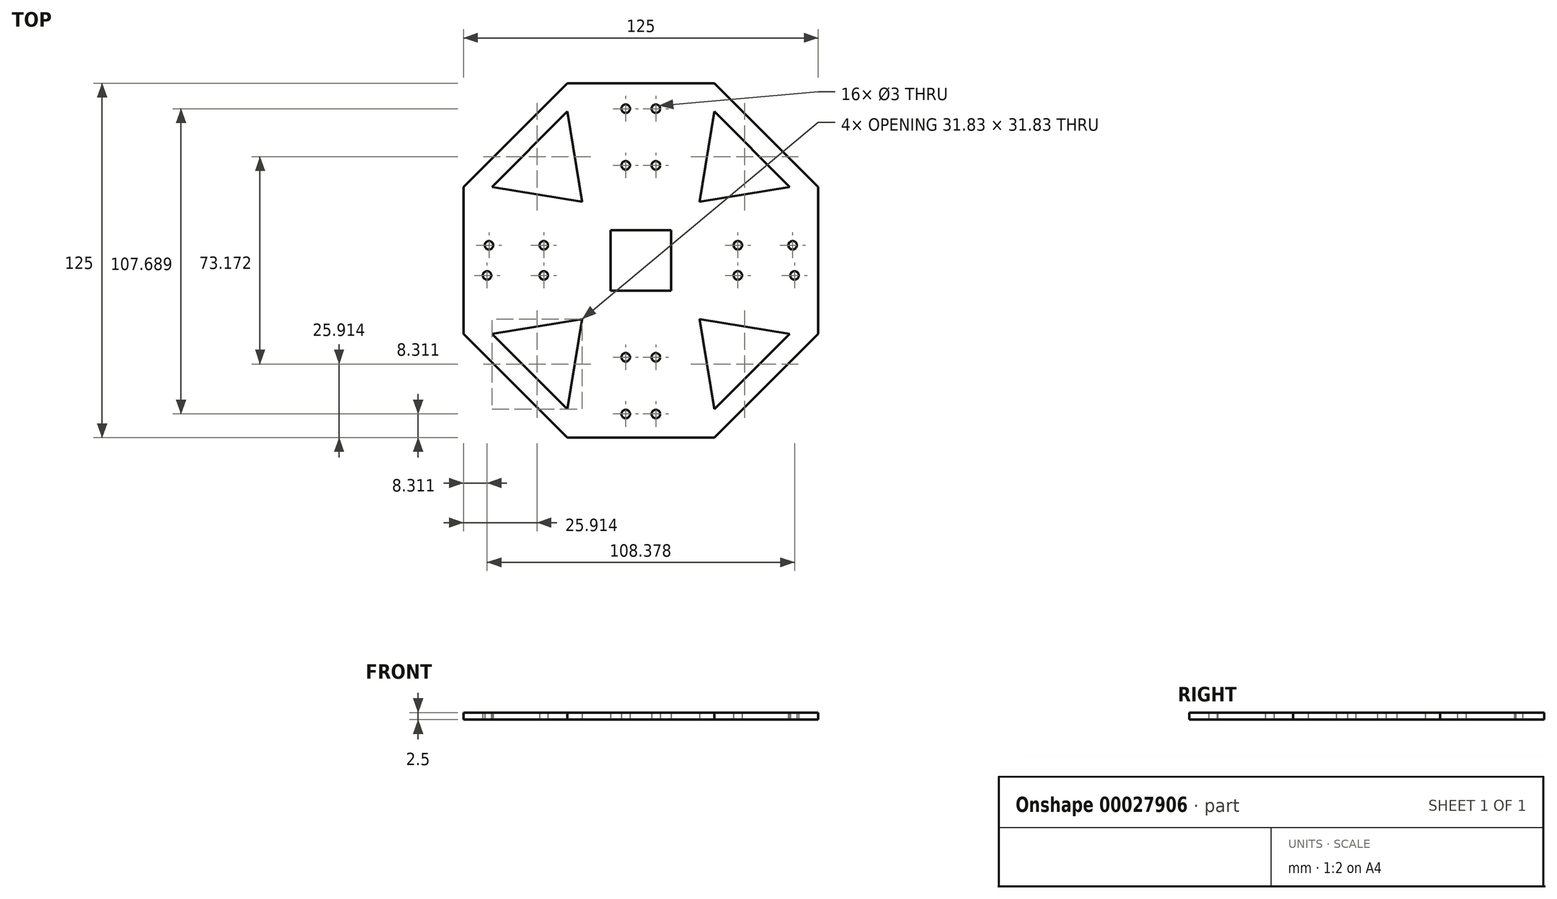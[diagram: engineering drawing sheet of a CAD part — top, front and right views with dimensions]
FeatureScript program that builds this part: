
annotation { "Feature Type Name" : "Feature", "Feature Type Description" : "" }
export const myFeature = defineFeature(function(context is Context, id is Id, definition is map)
    precondition{}
    {
        {
            var Q0;
            Q0=qCreatedBy(makeId("Top.planeOp"),FACE);
            var sketch = newSketch(context, id + "F0", { "sketchPlane" : qUnion([Q0])});
            skCircle(sketch, "E0.cCircle", {"center": v(0, 0) * mm, "radius": 62.5 * mm, "construction": true});
            skLineSegment(sketch, "E0.0", {"start": v(-25.89, 62.5) * mm, "end": v(25.89, 62.5) * mm});
            skLineSegment(sketch, "E0.1", {"start": v(25.89, 62.5) * mm, "end": v(62.5, 25.89) * mm});
            skLineSegment(sketch, "E0.2", {"start": v(62.5, 25.89) * mm, "end": v(62.5, -25.89) * mm});
            skLineSegment(sketch, "E0.3", {"start": v(62.5, -25.89) * mm, "end": v(25.89, -62.5) * mm});
            skLineSegment(sketch, "E0.4", {"start": v(25.89, -62.5) * mm, "end": v(-25.89, -62.5) * mm});
            skLineSegment(sketch, "E0.5", {"start": v(-25.89, -62.5) * mm, "end": v(-62.5, -25.89) * mm});
            skLineSegment(sketch, "E0.6", {"start": v(-62.5, -25.89) * mm, "end": v(-62.5, 25.89) * mm});
            skLineSegment(sketch, "E0.7", {"start": v(-62.5, 25.89) * mm, "end": v(-25.89, 62.5) * mm});
            skPoint(sketch, "E0.0.midPoint", {"position": v(0, 62.5) * mm});
            skLineSegment(sketch, "E1.rect.bottom", {"start": v(10.67, 10.67) * mm, "end": v(-10.67, 10.67) * mm});
            skLineSegment(sketch, "E1.rect.top", {"start": v(10.67, -10.67) * mm, "end": v(-10.67, -10.67) * mm});
            skLineSegment(sketch, "E1.rect.left", {"start": v(10.67, 10.67) * mm, "end": v(10.67, -10.67) * mm});
            skLineSegment(sketch, "E1.rect.right", {"start": v(-10.67, 10.67) * mm, "end": v(-10.67, -10.67) * mm});
            skLineSegment(sketch, "E2", {"start": v(-10.67, 20.67) * mm, "end": v(-10.67, 52.5) * mm});
            skLineSegment(sketch, "E3", {"start": v(-10.67, -52.5) * mm, "end": v(-10.67, -20.67) * mm});
            skLineSegment(sketch, "E4", {"start": v(-10.67, -20.67) * mm, "end": v(-20.67, -10.67) * mm});
            skLineSegment(sketch, "E5", {"start": v(-20.67, -10.67) * mm, "end": v(-20.67, 9.38) * mm});
            skLineSegment(sketch, "E6", {"start": v(-20.67, 9.38) * mm, "end": v(-10.67, 20.67) * mm});
            skLineSegment(sketch, "E7.1.3", {"start": v(10.67, 52.5) * mm, "end": v(10.67, 20.67) * mm});
            skLineSegment(sketch, "E7.1.4", {"start": v(10.67, 20.67) * mm, "end": v(20.67, 10.67) * mm});
            skLineSegment(sketch, "E7.1.5", {"start": v(20.67, 10.67) * mm, "end": v(20.67, -9.38) * mm});
            skLineSegment(sketch, "E7.1.6", {"start": v(20.67, -9.38) * mm, "end": v(10.67, -20.67) * mm});
            skLineSegment(sketch, "E7.1.7", {"start": v(10.67, -20.67) * mm, "end": v(10.67, -52.5) * mm});
            skLineSegment(sketch, "E8", {"start": v(0, 0) * mm, "end": v(0, -60.07) * mm, "construction": true});
            skLineSegment(sketch, "E9", {"start": v(0, -77.84) * mm, "end": v(0, 78.09) * mm, "construction": true});
            skLineSegment(sketch, "E10", {"start": v(0, 0) * mm, "end": v(98.82, 0) * mm, "construction": true});
            skPoint(sketch, "E10.endSnap0", {"position": v(62.5, 0) * mm});
            skLineSegment(sketch, "E11", {"start": v(98.82, 0) * mm, "end": v(-127.93, 0) * mm, "construction": true});
            skCircle(sketch, "E12", {"center": v(-5.32, -54.19) * mm, "radius": 1.5 * mm});
            skCircle(sketch, "E13.MirrorC", {"center": v(5.32, -54.19) * mm, "radius": 1.5 * mm});
            skCircle(sketch, "E14.0.1.0", {"center": v(-5.32, -34.19) * mm, "radius": 1.5 * mm});
            skCircle(sketch, "E14.0.1.1", {"center": v(5.32, -34.19) * mm, "radius": 1.5 * mm});
            skCircle(sketch, "E15.1.0", {"center": v(34.19, 5.32) * mm, "radius": 1.5 * mm});
            skCircle(sketch, "E15.1.1", {"center": v(34.19, -5.32) * mm, "radius": 1.5 * mm});
            skCircle(sketch, "E15.1.2", {"center": v(53.5, 5.32) * mm, "radius": 1.5 * mm});
            skCircle(sketch, "E15.1.3", {"center": v(54.19, -5.32) * mm, "radius": 1.5 * mm});
            skLineSegment(sketch, "E15.1.4", {"start": v(78.86, 3.3) * mm, "end": v(10.67, 1.61) * mm, "construction": true});
            skLineSegment(sketch, "E15.2.4", {"start": v(-0.92, 80.21) * mm, "end": v(2.96, -75.67) * mm, "construction": true});
            skLineSegment(sketch, "E15.3.4", {"start": v(-77.84, 1.03) * mm, "end": v(78.09, 1.03) * mm, "construction": true});
            skPoint(sketch, "E15.center", {"position": v(0.51, 0) * mm});
            skPoint(sketch, "E15.2.3.center.orphan", {"position": v(7.62, 55.69) * mm});
            skLineSegment(sketch, "E16.trimOffspring", {"start": v(1.04, 1.37) * mm, "end": v(-77.02, -0.57) * mm, "construction": true});
            skCircle(sketch, "E17.MirrorC", {"center": v(-34.19, 5.32) * mm, "radius": 1.5 * mm});
            skCircle(sketch, "E18.MirrorC", {"center": v(-53.5, 5.32) * mm, "radius": 1.5 * mm});
            skCircle(sketch, "E19.MirrorC", {"center": v(-54.19, -5.32) * mm, "radius": 1.5 * mm});
            skCircle(sketch, "E20.MirrorC", {"center": v(-34.19, -5.32) * mm, "radius": 1.5 * mm});
            skCircle(sketch, "E21", {"center": v(-5.32, 53.5) * mm, "radius": 1.5 * mm});
            skPoint(sketch, "E22.MirrorC.center.orphan", {"position": v(6.6, 53.16) * mm});
            skCircle(sketch, "E23.MirrorC", {"center": v(5.32, 53.5) * mm, "radius": 1.5 * mm});
            skCircle(sketch, "E24.0.1.0", {"center": v(-5.32, 33.5) * mm, "radius": 1.5 * mm});
            skCircle(sketch, "E24.0.1.1", {"center": v(5.32, 33.5) * mm, "radius": 1.5 * mm});
            skLineSegment(sketch, "E24.direction1", {"start": v(-5.32, 53.5) * mm, "end": v(18.4, 53.5) * mm, "construction": true});
            skLineSegment(sketch, "E24.direction2", {"start": v(-5.32, 53.5) * mm, "end": v(-5.32, 33.5) * mm, "construction": true});
            skLineSegment(sketch, "E25", {"start": v(-52.5, -25.89) * mm, "end": v(-25.89, -52.5) * mm});
            skLineSegment(sketch, "E26", {"start": v(-25.89, -52.5) * mm, "end": v(-20.67, -20.67) * mm});
            skLineSegment(sketch, "E27", {"start": v(-20.67, -20.67) * mm, "end": v(-52.5, -25.89) * mm});
            skLineSegment(sketch, "E28.1.0", {"start": v(25.89, -52.5) * mm, "end": v(52.5, -25.89) * mm});
            skLineSegment(sketch, "E28.1.1", {"start": v(52.5, -25.89) * mm, "end": v(20.67, -20.67) * mm});
            skLineSegment(sketch, "E28.1.2", {"start": v(20.67, -20.67) * mm, "end": v(25.89, -52.5) * mm});
            skLineSegment(sketch, "E28.2.0", {"start": v(52.5, 25.89) * mm, "end": v(25.89, 52.5) * mm});
            skLineSegment(sketch, "E28.2.1", {"start": v(25.89, 52.5) * mm, "end": v(20.67, 20.67) * mm});
            skLineSegment(sketch, "E28.2.2", {"start": v(20.67, 20.67) * mm, "end": v(52.5, 25.89) * mm});
            skLineSegment(sketch, "E28.3.0", {"start": v(-25.89, 52.5) * mm, "end": v(-52.5, 25.89) * mm});
            skLineSegment(sketch, "E28.3.1", {"start": v(-52.5, 25.89) * mm, "end": v(-20.67, 20.67) * mm});
            skLineSegment(sketch, "E28.3.2", {"start": v(-20.67, 20.67) * mm, "end": v(-25.89, 52.5) * mm});
            skSolve(sketch);
        }
        {
            var Q0;
            Q0=makeQuery(id+"F0.imprint","IMPRINT",FACE,{"disambiguationData":[TD([[makeQuery(id+"F0.imprint","IMPRINT",EDGE,{"derivedFrom":sQuery(id+"F0.wireOp",EDGE,"E0.0")}),-1.0]])]});
            var Q1;
            Q1=makeQuery(id+"F0.imprint","IMPRINT",FACE,{"disambiguationData":[TD([[makeQuery(id+"F0.imprint","IMPRINT",EDGE,{"derivedFrom":sQuery(id+"F0.wireOp",EDGE,"E5")}),1.0]])]});
            var Q2;
            Q2=makeQuery(id+"F0.imprint","IMPRINT",FACE,{"disambiguationData":[TD([[makeQuery(id+"F0.imprint","IMPRINT",EDGE,{"derivedFrom":sQuery(id+"F0.wireOp",EDGE,"E7.1.5")}),1.0]])]});
            extrude(context, id + "F1", {"entities" : qUnion([Q0, Q1, Q2]), "depth" : 2.5 * mm});
        }
    });
